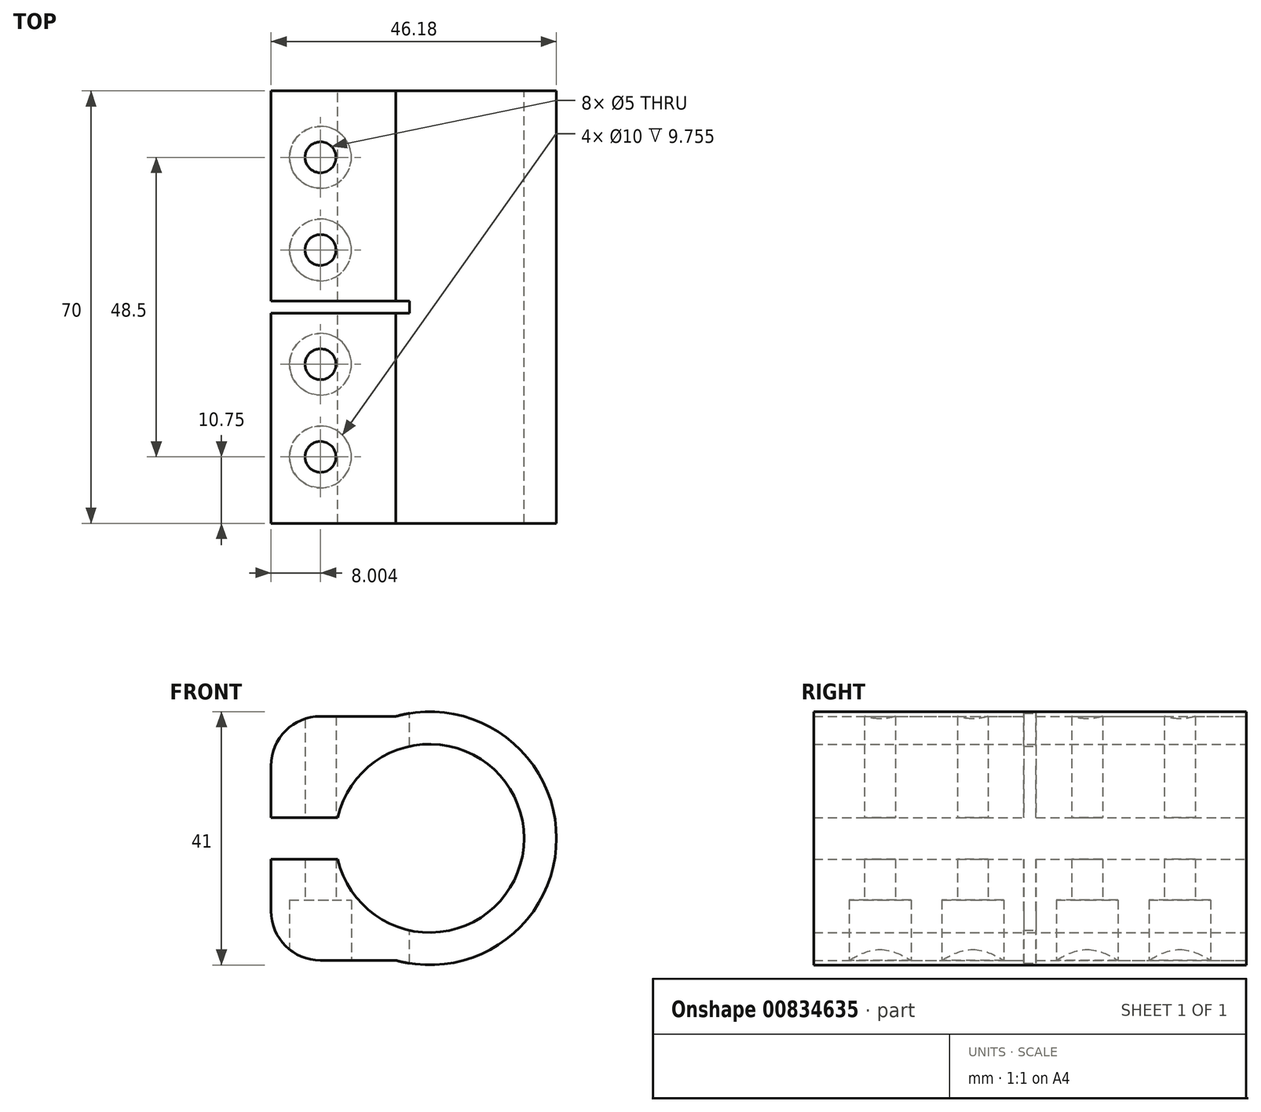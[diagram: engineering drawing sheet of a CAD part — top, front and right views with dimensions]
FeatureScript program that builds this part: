
annotation { "Feature Type Name" : "Feature", "Feature Type Description" : "" }
export const myFeature = defineFeature(function(context is Context, id is Id, definition is map)
    precondition{}
    {
        {
            var Q0;
            Q0=qCreatedBy(makeId("Front.planeOp"),FACE);
            var sketch = newSketch(context, id + "F0", { "sketchPlane" : qUnion([Q0])});
            skArc(sketch, "E0", {"start": v(-14.88, -3.35) * mm, "mid": v(15.25, 0) * mm, "end": v(-14.88, 3.35) * mm});
            skArc(sketch, "E1", {"start": v(-5.48, -19.75) * mm, "mid": v(20.5, 0) * mm, "end": v(-5.48, 19.75) * mm});
            skPoint(sketch, "E2.visualSharp", {"position": v(-26.05, 16.4) * mm});
            skPoint(sketch, "E3.start.orphan", {"position": v(-15.25, 0) * mm});
            skPoint(sketch, "E4.start.orphan", {"position": v(-26.05, 0) * mm});
            skPoint(sketch, "E2.filletArc.end.orphan", {"position": v(-26.05, 8.4) * mm});
            skLineSegment(sketch, "E5", {"start": v(-14.88, 3.35) * mm, "end": v(-25.68, 3.35) * mm});
            skLineSegment(sketch, "E6", {"start": v(-25.68, 3.35) * mm, "end": v(-25.68, 11.75) * mm});
            skLineSegment(sketch, "E7", {"start": v(-17.68, 19.75) * mm, "end": v(-5.48, 19.75) * mm});
            skPoint(sketch, "E8.visualSharp", {"position": v(-25.68, 19.75) * mm});
            skArc(sketch, "E8.filletArc", {"start": v(-17.68, 19.75) * mm, "mid": v(-23.33, 17.41) * mm, "end": v(-25.68, 11.75) * mm});
            skLineSegment(sketch, "E9.MirrorCS", {"start": v(-14.88, -3.35) * mm, "end": v(-25.68, -3.35) * mm});
            skLineSegment(sketch, "E10.MirrorCS", {"start": v(-25.68, -3.35) * mm, "end": v(-25.68, -11.75) * mm});
            skArc(sketch, "E11.MirrorCS", {"start": v(-17.68, -19.75) * mm, "mid": v(-23.33, -17.41) * mm, "end": v(-25.68, -11.75) * mm});
            skLineSegment(sketch, "E12.MirrorCS", {"start": v(-17.68, -19.75) * mm, "end": v(-5.48, -19.75) * mm});
            skPoint(sketch, "E13.orphan", {"position": v(-4.03, 0) * mm});
            skSolve(sketch);
        }
        {
            var Q0;
            Q0=makeQuery(id+"F0.imprint","IMPRINT",FACE,{"disambiguationData":[TD([[makeQuery(id+"F0.imprint","IMPRINT",EDGE,{"derivedFrom":sQuery(id+"F0.wireOp",EDGE,"E0")}),-1.0]])]});
            extrude(context, id + "F1", {"entities" : qUnion([Q0]), "endBound" : BoundingType.SYMMETRIC, "depth" : 70 * mm, "offsetDistance" : 25 * mm});
        }
        {
            var Q0;
            Q0=makeQuery(id+"F1.opExtrude","SWEPT_FACE",FACE,{"disambiguationData":[OSD([sQuery(id+"F0.wireOp",EDGE,"E12.MirrorCS")])]});
            var sketch = newSketch(context, id + "F2", { "sketchPlane" : qUnion([Q0])});
            skPoint(sketch, "E14", {"position": v(-17.68, 24.25) * mm});
            skPoint(sketch, "E15", {"position": v(-17.68, 9.25) * mm});
            skPoint(sketch, "E16", {"position": v(-17.68, -9.25) * mm});
            skPoint(sketch, "E17", {"position": v(-17.68, -24.25) * mm});
            skSolve(sketch);
        }
        {
            var Q0;
            Q0=sQuery(id+"F2.wireOp",VERTEX,"E14");
            var Q1;
            Q1=sQuery(id+"F2.wireOp",VERTEX,"E15");
            var Q2;
            Q2=sQuery(id+"F2.wireOp",VERTEX,"E16");
            var Q3;
            Q3=sQuery(id+"F2.wireOp",VERTEX,"E17");
            var Q4;
            Q4=makeQuery(id+"F1.opExtrude","SWEPT_BODY",BODY,{"disambiguationData":[OSD([sQuery(id+"F0.wireOp",EDGE,"E0"),sQuery(id+"F0.wireOp",EDGE,"E1"),sQuery(id+"F0.wireOp",EDGE,"E5"),sQuery(id+"F0.wireOp",EDGE,"E6"),sQuery(id+"F0.wireOp",EDGE,"E7"),sQuery(id+"F0.wireOp",EDGE,"E8.filletArc"),sQuery(id+"F0.wireOp",EDGE,"E9.MirrorCS"),sQuery(id+"F0.wireOp",EDGE,"E10.MirrorCS"),sQuery(id+"F0.wireOp",EDGE,"E11.MirrorCS"),sQuery(id+"F0.wireOp",EDGE,"E12.MirrorCS")])]});
            hole(context, id + "F3", {"style" : HoleStyle.C_BORE, "endStyle" : HoleEndStyle.THROUGH, "holeDiameter" : 5 * mm, "cBoreDiameter" : 10 * mm, "cBoreDepth" : 8 * mm, "majorDiameter" : 5 * mm, "isTappedThrough" : true, "tappedDepth" : 12 * mm, "tapClearance" : 3, "locations" : qUnion([Q0, Q1, Q2, Q3]), "scope" : qUnion([Q4])});
        }
        {
            var Q0;
            Q0=qCreatedBy(makeId("Top.planeOp"),FACE);
            var sketch = newSketch(context, id + "F4", { "sketchPlane" : qUnion([Q0])});
            skLineSegment(sketch, "E18.bottom", {"start": v(-25.68, -1) * mm, "end": v(-3.28, -1) * mm});
            skLineSegment(sketch, "E18.top", {"start": v(-25.68, 1) * mm, "end": v(-3.28, 1) * mm});
            skLineSegment(sketch, "E18.left", {"start": v(-25.68, -1) * mm, "end": v(-25.68, 1) * mm});
            skLineSegment(sketch, "E18.right", {"start": v(-3.28, -1) * mm, "end": v(-3.28, 1) * mm});
            skSolve(sketch);
        }
        {
            var Q0;
            Q0 = qSketchRegion(id + "F4", true);
            extrude(context, id + "F5", {"entities" : qUnion([Q0]), "operationType" : NewBodyOperationType.REMOVE, "endBound" : BoundingType.SYMMETRIC, "oppositeDirection" : true, "depth" : 50 * mm, "offsetDistance" : 25 * mm});
        }
    });
